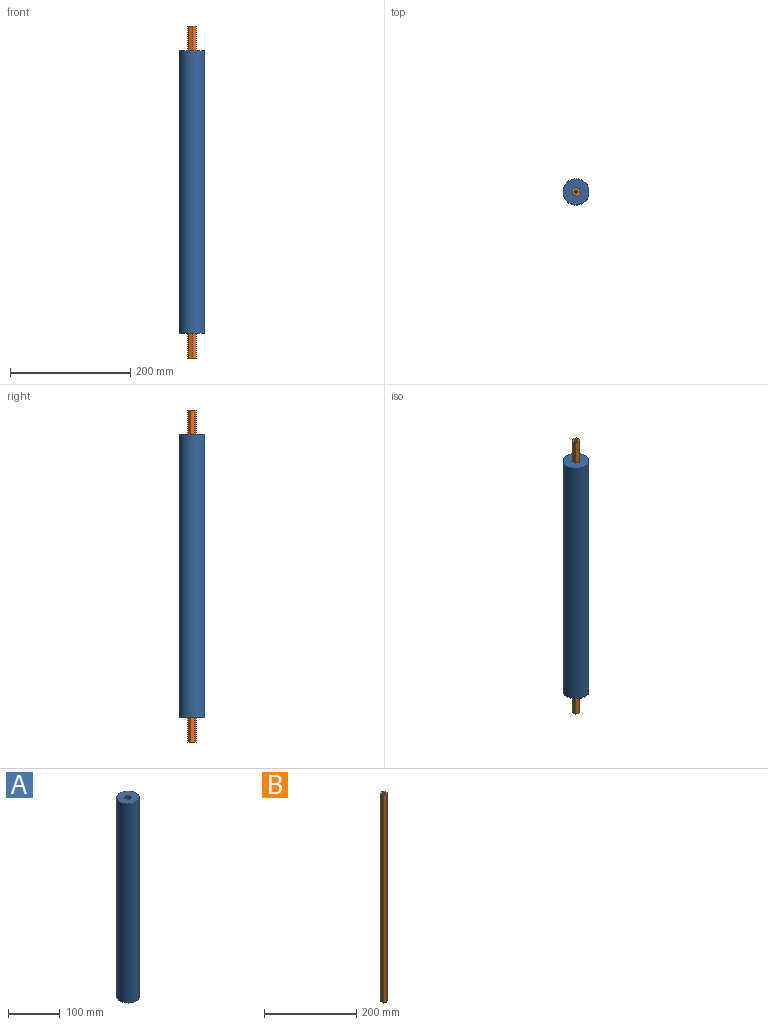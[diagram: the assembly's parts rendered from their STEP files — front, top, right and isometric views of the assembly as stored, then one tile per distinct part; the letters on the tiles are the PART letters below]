
ASSEMBLY  parts=2 mates=1
PART A: 9 faces, bbox 43.2x43.2x469.9 mm
  f0: plane 469.9x7.32mm, normal (-1,-0.07,0), area 3445.5mm2, adj f1,f5,f7,f8
  f1: plane 469.9x6.09mm, normal (-0.56,0.83,0), area 3445.5mm2, adj f0,f2,f7,f8
  f2: plane 469.9x6.58mm, normal (0.44,0.9,0), area 3445.5mm2, adj f1,f3,f7,f8
  f3: plane 469.9x7.32mm, normal (1,0.07,0), area 3445.5mm2, adj f2,f4,f7,f8
  f4: plane 469.9x6.09mm, normal (0.56,-0.83,0), area 3445.5mm2, adj f3,f5,f7,f8
  f5: plane 469.9x6.58mm, normal (-0.44,-0.9,0), area 3445.5mm2, adj f0,f4,f7,f8
  f6: cylinder r=21.59mm len=469.9mm, axis (0,0,-1), area 63743.8mm2, adj f7,f8
  f7: plane 43.18x43.18mm, normal (0,0,1), area 1324.7mm2, adj f0,f1,f2,f3,f4,f5,f6
  f8: plane 43.18x43.18mm, normal (0,0,-1), area 1324.7mm2, adj f0,f1,f2,f3,f4,f5,f6
PART B: 9 faces, bbox 13.5x14.5x552.5 mm
  f0: plane 552.45x7.27mm, normal (0.99,0.13,0), area 4050.8mm2, adj f1,f6,f7,f8
  f1: plane 552.45x6.76mm, normal (0.39,0.92,0), area 4050.8mm2, adj f0,f2,f7,f8
  f2: plane 552.45x5.84mm, normal (-0.61,0.8,0), area 4050.8mm2, adj f1,f3,f7,f8
  f3: plane 552.45x7.27mm, normal (-0.99,-0.13,0), area 4050.8mm2, adj f2,f4,f7,f8
  f4: plane 552.45x6.76mm, normal (-0.39,-0.92,0), area 4050.8mm2, adj f3,f6,f7,f8
  f5: cylinder r=2.55mm len=552.45mm, axis (0,0,-1), area 8860.8mm2, adj f7,f8
  f6: plane 552.45x5.84mm, normal (0.61,-0.8,0), area 4050.8mm2, adj f0,f4,f7,f8
  f7: plane 14.55x13.52mm, normal (0,0,1), area 119.2mm2, adj f0,f1,f2,f3,f4,f5,f6
  f8: plane 14.55x13.52mm, normal (0,0,-1), area 119.2mm2, adj f0,f1,f2,f3,f4,f5,f6
PLACE A rot(axis=(0,0,1),3.4deg) t=(-91.59,75.9,-72.16)mm
PLACE B rot(axis=(0,0,1),3.4deg) t=(-60.81,76.07,-113.43)mm
MATE fastened B.f5 <-> A.f6  axis (0,0,-1) through (-117.86,130.55,162.79)mm
